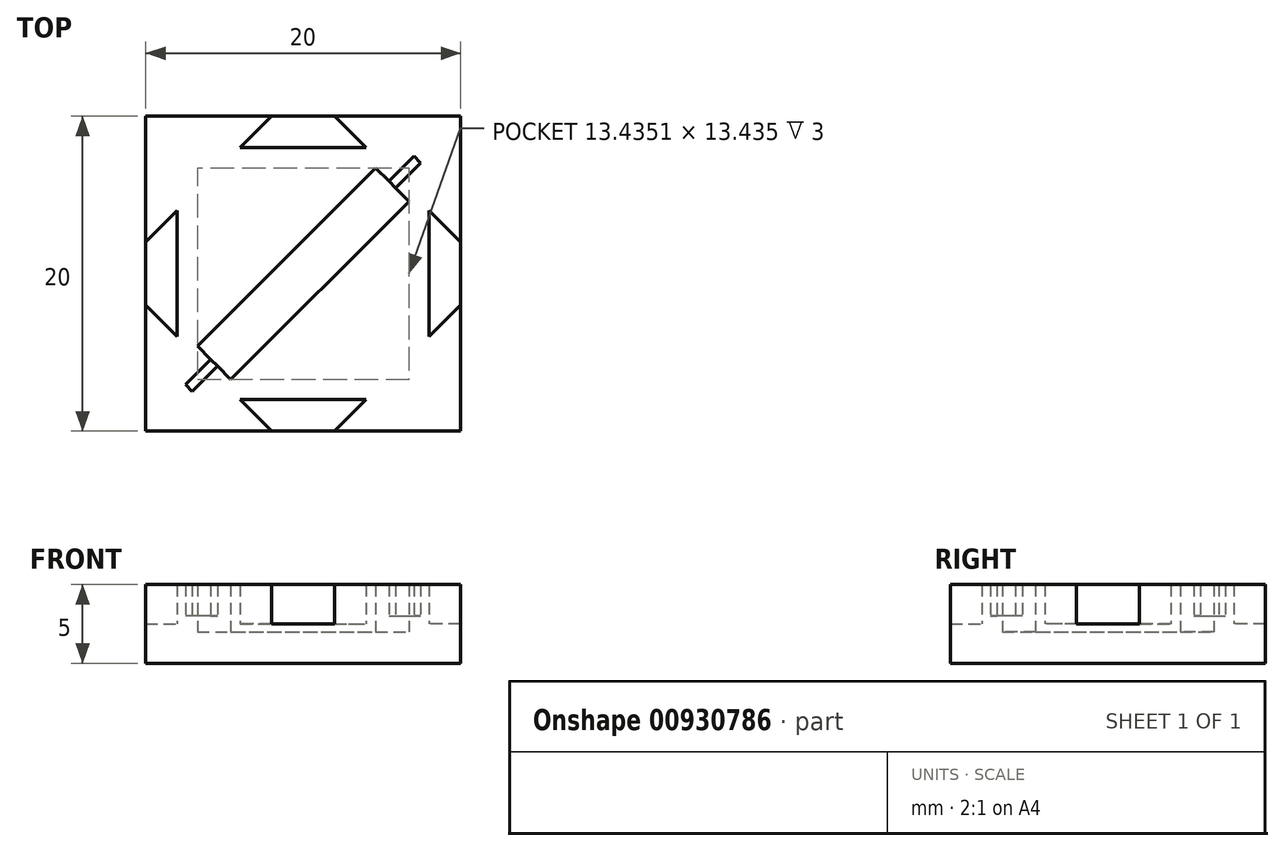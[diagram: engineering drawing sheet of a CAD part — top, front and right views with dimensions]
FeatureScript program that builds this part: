
annotation { "Feature Type Name" : "Feature", "Feature Type Description" : "" }
export const myFeature = defineFeature(function(context is Context, id is Id, definition is map)
    precondition{}
    {
        {
            var Q0;
            Q0=qCreatedBy(makeId("Top.planeOp"),FACE);
            var sketch = newSketch(context, id + "F0", { "sketchPlane" : qUnion([Q0])});
            skLineSegment(sketch, "E0.bottom", {"start": v(-19.97, 13.46) * mm, "end": v(0.03, 13.46) * mm});
            skLineSegment(sketch, "E0.top", {"start": v(-19.97, -6.54) * mm, "end": v(0.03, -6.54) * mm});
            skLineSegment(sketch, "E0.left", {"start": v(-19.97, 13.46) * mm, "end": v(-19.97, -6.54) * mm});
            skLineSegment(sketch, "E0.right", {"start": v(0.03, 13.46) * mm, "end": v(0.03, -6.54) * mm});
            skLineSegment(sketch, "E1.0", {"start": v(-17.97, 11.46) * mm, "end": v(-1.97, 11.46) * mm});
            skLineSegment(sketch, "E1.1", {"start": v(-17.97, 11.46) * mm, "end": v(-17.97, -4.54) * mm});
            skLineSegment(sketch, "E1.2", {"start": v(-17.97, -4.54) * mm, "end": v(-1.97, -4.54) * mm});
            skLineSegment(sketch, "E1.3", {"start": v(-1.97, 11.46) * mm, "end": v(-1.97, -4.54) * mm});
            skPoint(sketch, "E2", {"position": v(-9.97, 13.46) * mm});
            skPoint(sketch, "E3", {"position": v(-9.97, -6.54) * mm});
            skPoint(sketch, "E4", {"position": v(0.03, 3.46) * mm});
            skPoint(sketch, "E5", {"position": v(-19.97, 3.46) * mm});
            skPoint(sketch, "E6", {"position": v(-9.97, 11.46) * mm});
            skPoint(sketch, "E7", {"position": v(-1.97, 3.46) * mm});
            skPoint(sketch, "E8", {"position": v(-9.97, -4.54) * mm});
            skPoint(sketch, "E9", {"position": v(-17.97, 3.46) * mm});
            skLineSegment(sketch, "E10", {"start": v(-11.97, 13.46) * mm, "end": v(-13.97, 11.46) * mm});
            skLineSegment(sketch, "E11", {"start": v(-7.97, 13.46) * mm, "end": v(-5.97, 11.46) * mm});
            skLineSegment(sketch, "E12", {"start": v(0.03, 5.46) * mm, "end": v(-1.97, 7.46) * mm});
            skLineSegment(sketch, "E13", {"start": v(0.03, 1.46) * mm, "end": v(-1.97, -0.54) * mm});
            skLineSegment(sketch, "E14", {"start": v(-7.97, -6.54) * mm, "end": v(-5.97, -4.54) * mm});
            skLineSegment(sketch, "E15", {"start": v(-11.97, -6.54) * mm, "end": v(-13.97, -4.54) * mm});
            skLineSegment(sketch, "E16", {"start": v(-19.97, 1.46) * mm, "end": v(-17.97, -0.54) * mm});
            skLineSegment(sketch, "E17", {"start": v(-19.97, 5.46) * mm, "end": v(-17.97, 7.46) * mm});
            skLineSegment(sketch, "E18", {"start": v(-17.97, -2.42) * mm, "end": v(-4.1, 11.46) * mm});
            skLineSegment(sketch, "E19", {"start": v(-15.85, -4.54) * mm, "end": v(-1.97, 9.34) * mm});
            skPoint(sketch, "E20", {"position": v(-11.03, 4.52) * mm});
            skLineSegment(sketch, "E21", {"start": v(-16.69, -1.14) * mm, "end": v(-14.57, -3.26) * mm});
            skLineSegment(sketch, "E22", {"start": v(-5.38, 10.17) * mm, "end": v(-3.25, 8.05) * mm});
            skPoint(sketch, "E23", {"position": v(-15.63, -2.2) * mm});
            skLineSegment(sketch, "E24", {"start": v(-15.84, -1.99) * mm, "end": v(-17.97, -4.12) * mm});
            skLineSegment(sketch, "E25", {"start": v(-15.42, -2.41) * mm, "end": v(-17.55, -4.54) * mm});
            skPoint(sketch, "E26", {"position": v(-17.01, -4.01) * mm});
            skLineSegment(sketch, "E27", {"start": v(-17.01, -4.01) * mm, "end": v(-17.44, -3.59) * mm});
            skPoint(sketch, "E28", {"position": v(-4.31, 9.11) * mm});
            skLineSegment(sketch, "E29", {"start": v(-4.1, 8.9) * mm, "end": v(-1.97, 11.03) * mm});
            skLineSegment(sketch, "E30", {"start": v(-4.53, 9.33) * mm, "end": v(-2.4, 11.46) * mm});
            skPoint(sketch, "E31", {"position": v(-2.5, 10.5) * mm});
            skLineSegment(sketch, "E32", {"start": v(-2.5, 10.5) * mm, "end": v(-2.93, 10.92) * mm});
            skSolve(sketch);
        }
        {
            var Q0;
            {var subQ0=sQuery(id+"F0.wireOp",EDGE,"E1.0");var subQ5=sQuery(id+"F0.wireOp",EDGE,"E1.1");var subQ6=makeQuery(id+"F0.imprint","INTERSECT",VERTEX,{"derivedFrom":[subQ0,subQ5]});Q0=makeQuery(id+"F0.imprint","IMPRINT",FACE,{"disambiguationData":[TD([[makeQuery(id+"F0.imprint","IMPRINT",EDGE,{"disambiguationData":[TD([[subQ6,-1.0]])],"derivedFrom":subQ0}),-1.0]])]});}
            var Q1;
            {var subQ4=sQuery(id+"F0.wireOp",EDGE,"E18");var subQ5=sQuery(id+"F0.wireOp",EDGE,"E1.0");var subQ6=makeQuery(id+"F0.imprint","INTERSECT",VERTEX,{"derivedFrom":[subQ5,subQ4]});Q1=makeQuery(id+"F0.imprint","IMPRINT",FACE,{"disambiguationData":[TD([[makeQuery(id+"F0.imprint","IMPRINT",EDGE,{"disambiguationData":[TD([[subQ6,-1.0]])],"derivedFrom":subQ5}),-1.0]])]});}
            var Q2;
            {var subQ4=sQuery(id+"F0.wireOp",EDGE,"E19");var subQ6=sQuery(id+"F0.wireOp",EDGE,"E1.3");var subQ7=makeQuery(id+"F0.imprint","INTERSECT",VERTEX,{"derivedFrom":[subQ6,subQ4]});Q2=makeQuery(id+"F0.imprint","IMPRINT",FACE,{"disambiguationData":[TD([[makeQuery(id+"F0.imprint","IMPRINT",EDGE,{"disambiguationData":[TD([[subQ7,1.0]])],"derivedFrom":subQ6}),-1.0]])]});}
            var Q3;
            {var subQ1=sQuery(id+"F0.wireOp",EDGE,"E1.2");var subQ4=makeQuery(id+"F0.imprint","INTERSECT",VERTEX,{"derivedFrom":[subQ1,sQuery(id+"F0.wireOp",EDGE,"E15")]});Q3=makeQuery(id+"F0.imprint","IMPRINT",FACE,{"disambiguationData":[TD([[makeQuery(id+"F0.imprint","IMPRINT",EDGE,{"disambiguationData":[TD([[subQ4,1.0]])],"derivedFrom":subQ1}),1.0]])]});}
            var Q4;
            {var subQ4=sQuery(id+"F0.wireOp",EDGE,"E19");var subQ5=sQuery(id+"F0.wireOp",EDGE,"E1.2");var subQ6=makeQuery(id+"F0.imprint","INTERSECT",VERTEX,{"derivedFrom":[subQ5,subQ4]});Q4=makeQuery(id+"F0.imprint","IMPRINT",FACE,{"disambiguationData":[TD([[makeQuery(id+"F0.imprint","IMPRINT",EDGE,{"disambiguationData":[TD([[subQ6,1.0]])],"derivedFrom":subQ5}),1.0]])]});}
            var Q5;
            {var subQ4=sQuery(id+"F0.wireOp",EDGE,"E18");var subQ6=sQuery(id+"F0.wireOp",EDGE,"E1.1");var subQ7=makeQuery(id+"F0.imprint","INTERSECT",VERTEX,{"derivedFrom":[subQ6,subQ4]});Q5=makeQuery(id+"F0.imprint","IMPRINT",FACE,{"disambiguationData":[TD([[makeQuery(id+"F0.imprint","IMPRINT",EDGE,{"disambiguationData":[TD([[subQ7,-1.0]])],"derivedFrom":subQ6}),1.0]])]});}
            var Q6;
            {var subQ3=sQuery(id+"F0.wireOp",EDGE,"E32");Q6=makeQuery(id+"F0.imprint","IMPRINT",FACE,{"disambiguationData":[TD([[makeQuery(id+"F0.imprint","IMPRINT",EDGE,{"derivedFrom":subQ3}),-1.0]])]});}
            var Q7;
            {var subQ3=sQuery(id+"F0.wireOp",EDGE,"E27");Q7=makeQuery(id+"F0.imprint","IMPRINT",FACE,{"disambiguationData":[TD([[makeQuery(id+"F0.imprint","IMPRINT",EDGE,{"derivedFrom":subQ3}),1.0]])]});}
            var Q8;
            {var subQ3=sQuery(id+"F0.wireOp",EDGE,"E13");Q8=makeQuery(id+"F0.imprint","IMPRINT",FACE,{"disambiguationData":[TD([[makeQuery(id+"F0.imprint","IMPRINT",EDGE,{"derivedFrom":subQ3}),1.0]])]});}
            var Q9;
            {var subQ3=sQuery(id+"F0.wireOp",EDGE,"E11");Q9=makeQuery(id+"F0.imprint","IMPRINT",FACE,{"disambiguationData":[TD([[makeQuery(id+"F0.imprint","IMPRINT",EDGE,{"derivedFrom":subQ3}),1.0]])]});}
            var Q10;
            {var subQ7=sQuery(id+"F0.wireOp",EDGE,"E10");Q10=makeQuery(id+"F0.imprint","IMPRINT",FACE,{"disambiguationData":[TD([[makeQuery(id+"F0.imprint","IMPRINT",EDGE,{"derivedFrom":subQ7}),-1.0]])]});}
            var Q11;
            {var subQ7=sQuery(id+"F0.wireOp",EDGE,"E15");Q11=makeQuery(id+"F0.imprint","IMPRINT",FACE,{"disambiguationData":[TD([[makeQuery(id+"F0.imprint","IMPRINT",EDGE,{"derivedFrom":subQ7}),1.0]])]});}
            extrude(context, id + "F1", {"entities" : qUnion([Q0, Q1, Q2, Q3, Q4, Q5, Q6, Q7, Q8, Q9, Q10, Q11]), "depth" : 5 * mm, "offsetDistance" : 25 * mm});
        }
        {
            var Q0;
            {var subQ0=sQuery(id+"F0.wireOp",EDGE,"E21");var subQ7=sQuery(id+"F0.wireOp",EDGE,"E18");var subQ8=makeQuery(id+"F0.imprint","INTERSECT",VERTEX,{"derivedFrom":[subQ7,subQ0]});Q0=makeQuery(id+"F0.imprint","IMPRINT",FACE,{"disambiguationData":[TD([[makeQuery(id+"F0.imprint","IMPRINT",EDGE,{"disambiguationData":[TD([[subQ8,-1.0]])],"derivedFrom":subQ7}),-1.0]])]});}
            extrude(context, id + "F2", {"entities" : qUnion([Q0]), "operationType" : NewBodyOperationType.ADD, "depth" : 2 * mm, "offsetDistance" : 25 * mm});
        }
        {
            var Q0;
            {var subQ5=sQuery(id+"F0.wireOp",EDGE,"E27");Q0=makeQuery(id+"F0.imprint","IMPRINT",FACE,{"disambiguationData":[TD([[makeQuery(id+"F0.imprint","IMPRINT",EDGE,{"derivedFrom":subQ5}),-1.0]])]});}
            var Q1;
            {var subQ5=sQuery(id+"F0.wireOp",EDGE,"E32");Q1=makeQuery(id+"F0.imprint","IMPRINT",FACE,{"disambiguationData":[TD([[makeQuery(id+"F0.imprint","IMPRINT",EDGE,{"derivedFrom":subQ5}),1.0]])]});}
            extrude(context, id + "F3", {"entities" : qUnion([Q0, Q1]), "operationType" : NewBodyOperationType.ADD, "depth" : 3 * mm, "offsetDistance" : 25 * mm});
        }
        {
            var Q0;
            {var subQ0=sQuery(id+"F0.wireOp",EDGE,"E14");Q0=makeQuery(id+"F0.imprint","IMPRINT",FACE,{"disambiguationData":[TD([[makeQuery(id+"F0.imprint","IMPRINT",EDGE,{"derivedFrom":subQ0}),1.0]])]});}
            var Q1;
            {var subQ0=sQuery(id+"F0.wireOp",EDGE,"E16");Q1=makeQuery(id+"F0.imprint","IMPRINT",FACE,{"disambiguationData":[TD([[makeQuery(id+"F0.imprint","IMPRINT",EDGE,{"derivedFrom":subQ0}),1.0]])]});}
            var Q2;
            {var subQ0=sQuery(id+"F0.wireOp",EDGE,"E10");Q2=makeQuery(id+"F0.imprint","IMPRINT",FACE,{"disambiguationData":[TD([[makeQuery(id+"F0.imprint","IMPRINT",EDGE,{"derivedFrom":subQ0}),1.0]])]});}
            var Q3;
            {var subQ0=sQuery(id+"F0.wireOp",EDGE,"E12");Q3=makeQuery(id+"F0.imprint","IMPRINT",FACE,{"disambiguationData":[TD([[makeQuery(id+"F0.imprint","IMPRINT",EDGE,{"derivedFrom":subQ0}),1.0]])]});}
            extrude(context, id + "F4", {"entities" : qUnion([Q0, Q1, Q2, Q3]), "operationType" : NewBodyOperationType.ADD, "depth" : 2.5 * mm, "offsetDistance" : 25 * mm});
        }
    });
